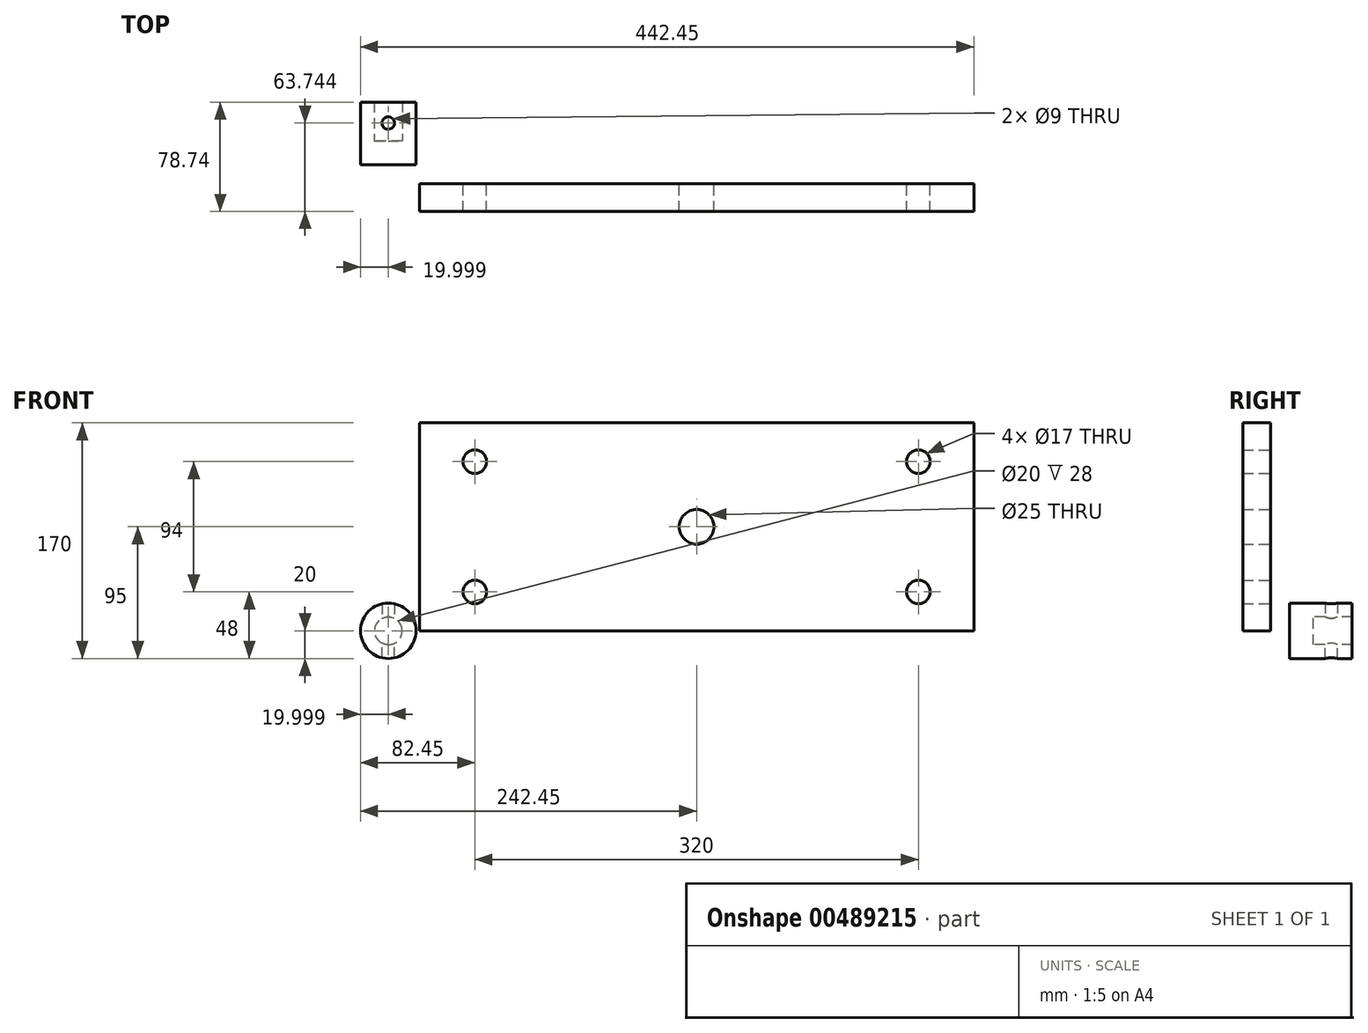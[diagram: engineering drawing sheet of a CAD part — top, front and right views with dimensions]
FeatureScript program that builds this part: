
annotation { "Feature Type Name" : "Feature", "Feature Type Description" : "" }
export const myFeature = defineFeature(function(context is Context, id is Id, definition is map)
    precondition{}
    {
        {
            var Q0;
            Q0=qCreatedBy(makeId("Front.planeOp"),FACE);
            var sketch = newSketch(context, id + "F0", { "sketchPlane" : qUnion([Q0])});
            skLineSegment(sketch, "E0.bottom", {"start": v(0, 0) * mm, "end": v(400, 0) * mm});
            skLineSegment(sketch, "E0.top", {"start": v(0, 150) * mm, "end": v(400, 150) * mm});
            skLineSegment(sketch, "E0.left", {"start": v(0, 0) * mm, "end": v(0, 150) * mm});
            skLineSegment(sketch, "E0.right", {"start": v(400, 0) * mm, "end": v(400, 150) * mm});
            skCircle(sketch, "E1", {"center": v(200, 75) * mm, "radius": 12.5 * mm});
            skPoint(sketch, "E1.centerSnap0", {"position": v(400, 75) * mm});
            skPoint(sketch, "E1.centerSnap1", {"position": v(200, 0) * mm});
            skLineSegment(sketch, "E2", {"start": v(200, 75) * mm, "end": v(0, 75) * mm, "construction": true});
            skPoint(sketch, "E3", {"position": v(40, 122) * mm});
            skPoint(sketch, "E4.MirrorP", {"position": v(40, 28) * mm});
            skLineSegment(sketch, "E5", {"start": v(200, 75) * mm, "end": v(200, 182.53) * mm, "construction": true});
            skPoint(sketch, "E5.endSnap0", {"position": v(200, 150) * mm});
            skPoint(sketch, "E6.MirrorP", {"position": v(360, 28) * mm});
            skPoint(sketch, "E7.MirrorP", {"position": v(360, 122) * mm});
            skSolve(sketch);
        }
        {
            var Q0;
            Q0=makeQuery(id+"F0.imprint","IMPRINT",FACE,{"disambiguationData":[TD([[makeQuery(id+"F0.imprint","IMPRINT",EDGE,{"derivedFrom":sQuery(id+"F0.wireOp",EDGE,"E0.bottom")}),1.0]])]});
            extrude(context, id + "F1", {"entities" : qUnion([Q0]), "depth" : 20 * mm, "offsetDistance" : 25 * mm});
        }
        {
            var Q0;
            Q0=qCreatedBy(makeId("Top.planeOp"),FACE);
            var sketch = newSketch(context, id + "F2", { "sketchPlane" : qUnion([Q0])});
            skLineSegment(sketch, "E8.bottom", {"start": v(-22.45, 13.74) * mm, "end": v(-42.45, 13.74) * mm});
            skLineSegment(sketch, "E8.top", {"start": v(-32.45, 58.74) * mm, "end": v(-42.45, 58.74) * mm});
            skLineSegment(sketch, "E8.left", {"start": v(-22.45, 13.74) * mm, "end": v(-22.45, 30.74) * mm});
            skLineSegment(sketch, "E8.right", {"start": v(-42.45, 13.74) * mm, "end": v(-42.45, 58.74) * mm});
            skLineSegment(sketch, "E9", {"start": v(-32.45, 58.74) * mm, "end": v(-32.45, 30.74) * mm});
            skLineSegment(sketch, "E10", {"start": v(-32.45, 30.74) * mm, "end": v(-22.45, 30.74) * mm});
            skPoint(sketch, "E11", {"position": v(-22.45, 43.74) * mm});
            skLineSegment(sketch, "E12.bottom", {"start": v(-22.45, 13.74) * mm, "end": v(-34.95, 13.74) * mm});
            skLineSegment(sketch, "E12.top", {"start": v(-22.45, -1.26) * mm, "end": v(-34.95, -1.26) * mm});
            skLineSegment(sketch, "E12.left", {"start": v(-22.45, 13.74) * mm, "end": v(-22.45, -1.26) * mm});
            skLineSegment(sketch, "E12.right", {"start": v(-34.95, 13.74) * mm, "end": v(-34.95, -1.26) * mm});
            skLineSegment(sketch, "E13.bottom", {"start": v(-22.45, -1.26) * mm, "end": v(-29.45, -1.26) * mm});
            skLineSegment(sketch, "E13.top", {"start": v(-22.45, -31.26) * mm, "end": v(-29.45, -31.26) * mm});
            skLineSegment(sketch, "E13.left", {"start": v(-22.45, -1.26) * mm, "end": v(-22.45, -31.26) * mm});
            skLineSegment(sketch, "E13.right", {"start": v(-29.45, -1.26) * mm, "end": v(-29.45, -31.26) * mm});
            skSolve(sketch);
        }
        {
            var Q0;
            Q0=makeQuery(id+"F2.imprint","IMPRINT",FACE,{"disambiguationData":[TD([[makeQuery(id+"F2.imprint","IMPRINT",EDGE,{"derivedFrom":sQuery(id+"F2.wireOp",EDGE,"E12.bottom")}),1.0]])]});
            var Q1;
            Q1=makeQuery(id+"F2.imprint","IMPRINT",FACE,{"disambiguationData":[TD([[makeQuery(id+"F2.imprint","IMPRINT",EDGE,{"derivedFrom":sQuery(id+"F2.wireOp",EDGE,"E8.bottom")}),-1.0]])]});
            var Q2;
            Q2=makeQuery(id+"F2.imprint","IMPRINT",FACE,{"disambiguationData":[TD([[makeQuery(id+"F2.imprint","IMPRINT",EDGE,{"derivedFrom":sQuery(id+"F2.wireOp",EDGE,"E13.bottom")}),1.0]])]});
            var Q3;
            Q3=sQuery(id+"F2.wireOp",EDGE,"E8.left");
            revolve(context, id + "F3", {"surfaceOperationType" : NewSurfaceOperationType.NEW, "entities" : qUnion([Q0, Q1, Q2]), "axis" : qUnion([Q3]), "revolveType" : RevolveType.FULL});
        }
        {
            var Q0;
            Q0=sQuery(id+"F2.wireOp",VERTEX,"E11");
            var Q1;
            Q1=makeQuery(id+"F3.opRevolve","SWEPT_BODY",BODY,{"disambiguationData":[OSD([sQuery(id+"F2.wireOp",EDGE,"E8.bottom"),sQuery(id+"F2.wireOp",EDGE,"E8.top"),sQuery(id+"F2.wireOp",EDGE,"E8.right"),sQuery(id+"F2.wireOp",EDGE,"E9"),sQuery(id+"F2.wireOp",EDGE,"E10"),sQuery(id+"F2.wireOp",EDGE,"E8.left"),sQuery(id+"F2.wireOp",EDGE,"E12.top"),sQuery(id+"F2.wireOp",EDGE,"E12.left"),sQuery(id+"F2.wireOp",EDGE,"E12.right")])]});
            hole(context, id + "F4", {"style" : HoleStyle.SIMPLE, "endStyle" : HoleEndStyle.THROUGH, "oppositeDirection" : true, "standardTappedOrClearance" : lookupTablePath({ "fit" : "Normal", "standard" : "ISO", "size" : "M8", "type" : "Clearance" }), "standardBlindInLast" : lookupTablePath({ "fit" : "Normal", "standard" : "ISO", "engagement" : "75%", "pitch" : "1.25 mm", "size" : "M8", "type" : "Clearance & tapped" }), "holeDiameter" : 9 * mm, "majorDiameter" : 5 * mm, "isTappedThrough" : true, "tappedDepth" : 12 * mm, "tapClearance" : 3, "startFromSketch" : true, "locations" : qUnion([Q0]), "scope" : qUnion([Q1])});
        }
        {
            var Q0;
            Q0=sQuery(id+"F2.wireOp",VERTEX,"E11");
            var Q1;
            Q1=makeQuery(id+"F3.opRevolve","SWEPT_BODY",BODY,{"disambiguationData":[OSD([sQuery(id+"F2.wireOp",EDGE,"E8.bottom"),sQuery(id+"F2.wireOp",EDGE,"E8.top"),sQuery(id+"F2.wireOp",EDGE,"E8.right"),sQuery(id+"F2.wireOp",EDGE,"E9"),sQuery(id+"F2.wireOp",EDGE,"E10"),sQuery(id+"F2.wireOp",EDGE,"E8.left"),sQuery(id+"F2.wireOp",EDGE,"E12.top"),sQuery(id+"F2.wireOp",EDGE,"E12.left"),sQuery(id+"F2.wireOp",EDGE,"E12.right")])]});
            hole(context, id + "F5", {"style" : HoleStyle.SIMPLE, "endStyle" : HoleEndStyle.THROUGH, "standardTappedOrClearance" : lookupTablePath({ "fit" : "Normal", "standard" : "ISO", "size" : "M8", "type" : "Clearance" }), "standardBlindInLast" : lookupTablePath({ "fit" : "Normal", "standard" : "ISO", "engagement" : "75%", "pitch" : "1.25 mm", "size" : "M8", "type" : "Clearance & tapped" }), "holeDiameter" : 9 * mm, "majorDiameter" : 5 * mm, "isTappedThrough" : true, "tappedDepth" : 12 * mm, "tapClearance" : 3, "startFromSketch" : true, "locations" : qUnion([Q0]), "scope" : qUnion([Q1])});
        }
        {
            var Q0;
            Q0=sQuery(id+"F0.wireOp",VERTEX,"E7.MirrorP");
            var Q1;
            Q1=sQuery(id+"F0.wireOp",VERTEX,"E6.MirrorP");
            var Q2;
            Q2=sQuery(id+"F0.wireOp",VERTEX,"E3");
            var Q3;
            Q3=sQuery(id+"F0.wireOp",VERTEX,"E4.MirrorP");
            var Q4;
            Q4=makeQuery(id+"F1.opExtrude","SWEPT_BODY",BODY,{"disambiguationData":[OSD([sQuery(id+"F0.wireOp",EDGE,"E0.bottom"),sQuery(id+"F0.wireOp",EDGE,"E0.top"),sQuery(id+"F0.wireOp",EDGE,"E0.left"),sQuery(id+"F0.wireOp",EDGE,"E0.right"),sQuery(id+"F0.wireOp",EDGE,"E1")])]});
            hole(context, id + "F6", {"style" : HoleStyle.SIMPLE, "endStyle" : HoleEndStyle.BLIND, "oppositeDirection" : true, "standardTappedOrClearance" : lookupTablePath({ "standard" : "ISO", "size" : "17", "type" : "Drilled" }), "standardBlindInLast" : lookupTablePath({ "standard" : "ISO", "size" : "17", "type" : "Drilled" }), "holeDiameter" : 17 * mm, "majorDiameter" : 16 * mm, "holeDepth" : 35 * mm, "isTappedThrough" : true, "tappedDepth" : 25 * mm, "tapClearance" : 5, "startFromSketch" : true, "locations" : qUnion([Q0, Q1, Q2, Q3]), "scope" : qUnion([Q4])});
        }
    });
